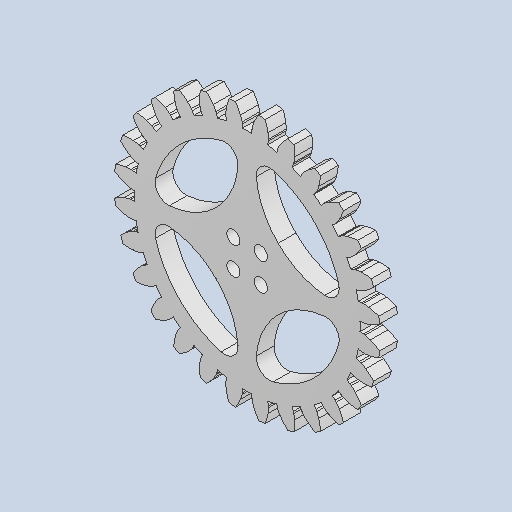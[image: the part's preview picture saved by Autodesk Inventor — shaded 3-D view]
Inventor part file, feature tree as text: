
AUTODESK INVENTOR PART (.ipt)
format: ipt  version: 2023 (Build 270158030, 158C)  size: 650,752 bytes
history: native  units: mm
features: extrude x3, sketch x3
ambient origin geometry x8: Origin, YZ Plane, XZ Plane, XY Plane, X Axis, Y Axis, Z Axis, Center Point
bodies: Solid1 (feature_tree)
feature tree (6):
  extrude  "Extrusion1"  Depth=3.0mm
  extrude  "Extrusion2"  Depth=6.2mm
  extrude  "Extrusion3"  Depth=4.0mm
  sketch  "Sketch1"  dims[d0=4.0mm d1=0.0mm d2=3.0mm]
  sketch  "Sketch2"  dims[d6=40.0mm d8=360.0deg d10=6.2mm]
  sketch  "Sketch3"  dims[d11=3.0mm d12=0.0mm d13=4.0mm d14=3.0mm d16=4.0mm d17=17.0mm d18=19.0mm d19=40.0mm d21=360.0deg d23=0.0mm d24=0.0mm]
